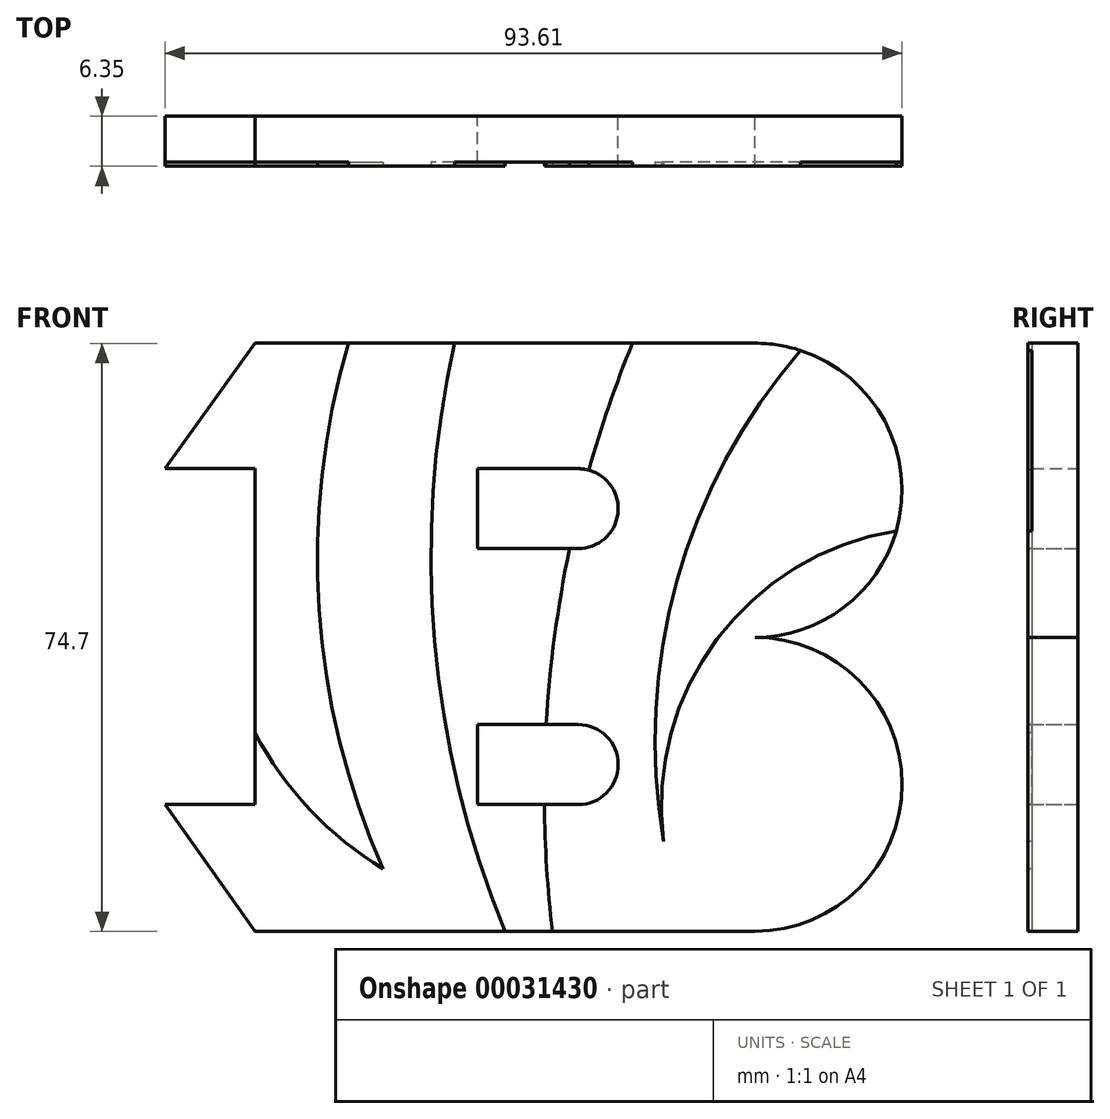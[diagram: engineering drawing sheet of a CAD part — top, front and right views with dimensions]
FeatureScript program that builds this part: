
annotation { "Feature Type Name" : "Feature", "Feature Type Description" : "" }
export const myFeature = defineFeature(function(context is Context, id is Id, definition is map)
    precondition{}
    {
        {
            var Q0;
            Q0=qCreatedBy(makeId("Front.planeOp"),FACE);
            var sketch = newSketch(context, id + "F0", { "sketchPlane" : qUnion([Q0])});
            skLineSegment(sketch, "E0.bottom", {"start": v(-55.8, 33.77) * mm, "end": v(7.7, 33.77) * mm});
            skLineSegment(sketch, "E0.top", {"start": v(-55.8, -40.93) * mm, "end": v(7.7, -40.93) * mm});
            skLineSegment(sketch, "E1", {"start": v(-55.8, 17.84) * mm, "end": v(-55.8, -24.82) * mm});
            skLineSegment(sketch, "E2", {"start": v(-55.8, 17.84) * mm, "end": v(-67.24, 17.84) * mm});
            skLineSegment(sketch, "E3", {"start": v(-55.8, -24.82) * mm, "end": v(-67.24, -24.82) * mm});
            skLineSegment(sketch, "E4", {"start": v(-67.24, 17.84) * mm, "end": v(-55.8, 33.77) * mm});
            skLineSegment(sketch, "E5", {"start": v(-67.24, -24.82) * mm, "end": v(-55.8, -40.93) * mm});
            skArc(sketch, "E6", {"start": v(7.7, -40.93) * mm, "mid": v(26.37, -22.25) * mm, "end": v(7.7, -3.58) * mm});
            skArc(sketch, "E7", {"start": v(7.7, -3.58) * mm, "mid": v(26.37, 15.1) * mm, "end": v(7.7, 33.77) * mm});
            skLineSegment(sketch, "E8", {"start": v(-27.54, 17.84) * mm, "end": v(-14.76, 17.84) * mm});
            skLineSegment(sketch, "E9", {"start": v(-27.54, -24.82) * mm, "end": v(-14.76, -24.82) * mm});
            skLineSegment(sketch, "E10", {"start": v(-27.54, -24.82) * mm, "end": v(-27.54, -14.66) * mm});
            skLineSegment(sketch, "E11", {"start": v(-27.54, -14.66) * mm, "end": v(-14.76, -14.66) * mm});
            skArc(sketch, "E12", {"start": v(-14.76, -24.82) * mm, "mid": v(-9.68, -19.74) * mm, "end": v(-14.76, -14.66) * mm});
            skLineSegment(sketch, "E13", {"start": v(-27.54, 17.84) * mm, "end": v(-27.54, 7.68) * mm});
            skLineSegment(sketch, "E14", {"start": v(-27.54, 7.68) * mm, "end": v(-14.76, 7.68) * mm});
            skArc(sketch, "E15", {"start": v(-14.76, 7.68) * mm, "mid": v(-9.68, 12.76) * mm, "end": v(-14.76, 17.84) * mm});
            skArc(sketch, "E16", {"start": v(-55.8, -11.8) * mm, "mid": v(-50.41, -24.58) * mm, "end": v(-40.33, -34.1) * mm});
            skArc(sketch, "E17", {"start": v(-44.63, 33.77) * mm, "mid": v(-46.3, -0.4) * mm, "end": v(-40.33, -34.1) * mm});
            skArc(sketch, "E18", {"start": v(-33.82, 33.77) * mm, "mid": v(-36.44, -4.06) * mm, "end": v(-27.54, -40.93) * mm});
            skPoint(sketch, "E19.endSnap0", {"position": v(-21.15, 17.84) * mm});
            skArc(sketch, "E20", {"start": v(-12.13, 33.77) * mm, "mid": v(-14.98, 25.9) * mm, "end": v(-17.32, 17.84) * mm});
            skArc(sketch, "E21", {"start": v(7.7, 33.77) * mm, "mid": v(-2.9, 3.42) * mm, "end": v(0.66, -28.53) * mm});
            skArc(sketch, "E22", {"start": v(24.63, 22.97) * mm, "mid": v(6.45, 0.1) * mm, "end": v(0.66, -28.53) * mm});
            skArc(sketch, "E23.trimOffspring", {"start": v(-19.47, 7.68) * mm, "mid": v(-20.86, -3.45) * mm, "end": v(-21.27, -14.66) * mm});
            skArc(sketch, "E24.trimOffspring", {"start": v(-20.8, -24.82) * mm, "mid": v(-19.83, -32.91) * mm, "end": v(-18.36, -40.93) * mm});
            skSolve(sketch);
        }
        {
            var Q0;
            {var subQ4=sQuery(id+"F0.wireOp",EDGE,"E3");Q0=makeQuery(id+"F0.imprint","IMPRINT",FACE,{"disambiguationData":[TD([[makeQuery(id+"F0.imprint","IMPRINT",EDGE,{"derivedFrom":subQ4}),1.0]])]});}
            var Q1;
            {var subQ11=sQuery(id+"F0.wireOp",EDGE,"E6");Q1=makeQuery(id+"F0.imprint","IMPRINT",FACE,{"disambiguationData":[TD([[makeQuery(id+"F0.imprint","IMPRINT",EDGE,{"derivedFrom":subQ11}),1.0]])]});}
            var Q2;
            {var subQ1=sQuery(id+"F0.wireOp",EDGE,"E21");Q2=makeQuery(id+"F0.imprint","IMPRINT",FACE,{"disambiguationData":[TD([[makeQuery(id+"F0.imprint","IMPRINT",EDGE,{"derivedFrom":subQ1}),1.0]])]});}
            var Q3;
            {var subQ7=sQuery(id+"F0.wireOp",EDGE,"E10");Q3=makeQuery(id+"F0.imprint","IMPRINT",FACE,{"disambiguationData":[TD([[makeQuery(id+"F0.imprint","IMPRINT",EDGE,{"derivedFrom":subQ7}),1.0]])]});}
            var Q4;
            {var subQ3=sQuery(id+"F0.wireOp",EDGE,"E2");Q4=makeQuery(id+"F0.imprint","IMPRINT",FACE,{"disambiguationData":[TD([[makeQuery(id+"F0.imprint","IMPRINT",EDGE,{"derivedFrom":subQ3}),-1.0]])]});}
            extrude(context, id + "F1", {"entities" : qUnion([Q0, Q1, Q2, Q3, Q4]), "depth" : 6.35 * mm});
        }
        {
            var Q0;
            Q0=makeQuery(id+"F1.opExtrude","CAP_FACE",FACE,{"disambiguationData":[OSD([sQuery(id+"F0.wireOp",EDGE,"E0.bottom"),sQuery(id+"F0.wireOp",EDGE,"E0.top"),sQuery(id+"F0.wireOp",EDGE,"E1"),sQuery(id+"F0.wireOp",EDGE,"E2"),sQuery(id+"F0.wireOp",EDGE,"E3"),sQuery(id+"F0.wireOp",EDGE,"E4"),sQuery(id+"F0.wireOp",EDGE,"E5"),sQuery(id+"F0.wireOp",EDGE,"E6"),sQuery(id+"F0.wireOp",EDGE,"E7"),sQuery(id+"F0.wireOp",EDGE,"E8"),sQuery(id+"F0.wireOp",EDGE,"E9"),sQuery(id+"F0.wireOp",EDGE,"E10"),sQuery(id+"F0.wireOp",EDGE,"E11"),sQuery(id+"F0.wireOp",EDGE,"E12"),sQuery(id+"F0.wireOp",EDGE,"E13"),sQuery(id+"F0.wireOp",EDGE,"E14"),sQuery(id+"F0.wireOp",EDGE,"E15")])],"isStart":false});
            var sketch = newSketch(context, id + "F2", { "sketchPlane" : qUnion([Q0])});
            skArc(sketch, "E25", {"start": v(-43.94, 33.77) * mm, "mid": v(-47.68, -0.01) * mm, "end": v(-39.52, -33.01) * mm});
            skArc(sketch, "E26", {"start": v(-55.8, -15.74) * mm, "mid": v(-48.83, -25.48) * mm, "end": v(-39.52, -33.01) * mm});
            skArc(sketch, "E27", {"start": v(-30.5, 33.77) * mm, "mid": v(-33, -4.07) * mm, "end": v(-24.06, -40.93) * mm});
            skArc(sketch, "E28", {"start": v(-7.87, 33.77) * mm, "mid": v(-17.68, -2.93) * mm, "end": v(-18.04, -40.93) * mm});
            skArc(sketch, "E29", {"start": v(25.64, 9.96) * mm, "mid": v(2.89, -3.8) * mm, "end": v(-3.93, -29.51) * mm});
            skArc(sketch, "E30", {"start": v(13.47, 32.86) * mm, "mid": v(-2.2, 3.62) * mm, "end": v(-3.93, -29.51) * mm});
            skSolve(sketch);
        }
        {
            var Q0;
            Q0 = qSketchRegion(id + "F2", true);
            var Q1;
            {var subQ4=sQuery(id+"F2.wireOp",EDGE,"E25");Q1=makeQuery(id+"F2.imprint","IMPRINT",FACE,{"disambiguationData":[TD([[makeQuery(id+"F2.imprint","IMPRINT",EDGE,{"derivedFrom":subQ4}),-1.0]])]});}
            var Q2;
            {var subQ12=sQuery(id+"F2.wireOp",EDGE,"E27");Q2=makeQuery(id+"F2.imprint","IMPRINT",FACE,{"disambiguationData":[TD([[makeQuery(id+"F2.imprint","IMPRINT",EDGE,{"derivedFrom":subQ12}),1.0]])]});}
            var Q3;
            {var subQ2=sQuery(id+"F2.wireOp",EDGE,"E29");Q3=makeQuery(id+"F2.imprint","IMPRINT",FACE,{"disambiguationData":[TD([[makeQuery(id+"F2.imprint","IMPRINT",EDGE,{"derivedFrom":subQ2}),-1.0]])]});}
            extrude(context, id + "F3", {"entities" : qUnion([Q0, Q1, Q2, Q3]), "operationType" : NewBodyOperationType.REMOVE, "oppositeDirection" : true, "depth" : 0.5 * mm});
        }
    });
